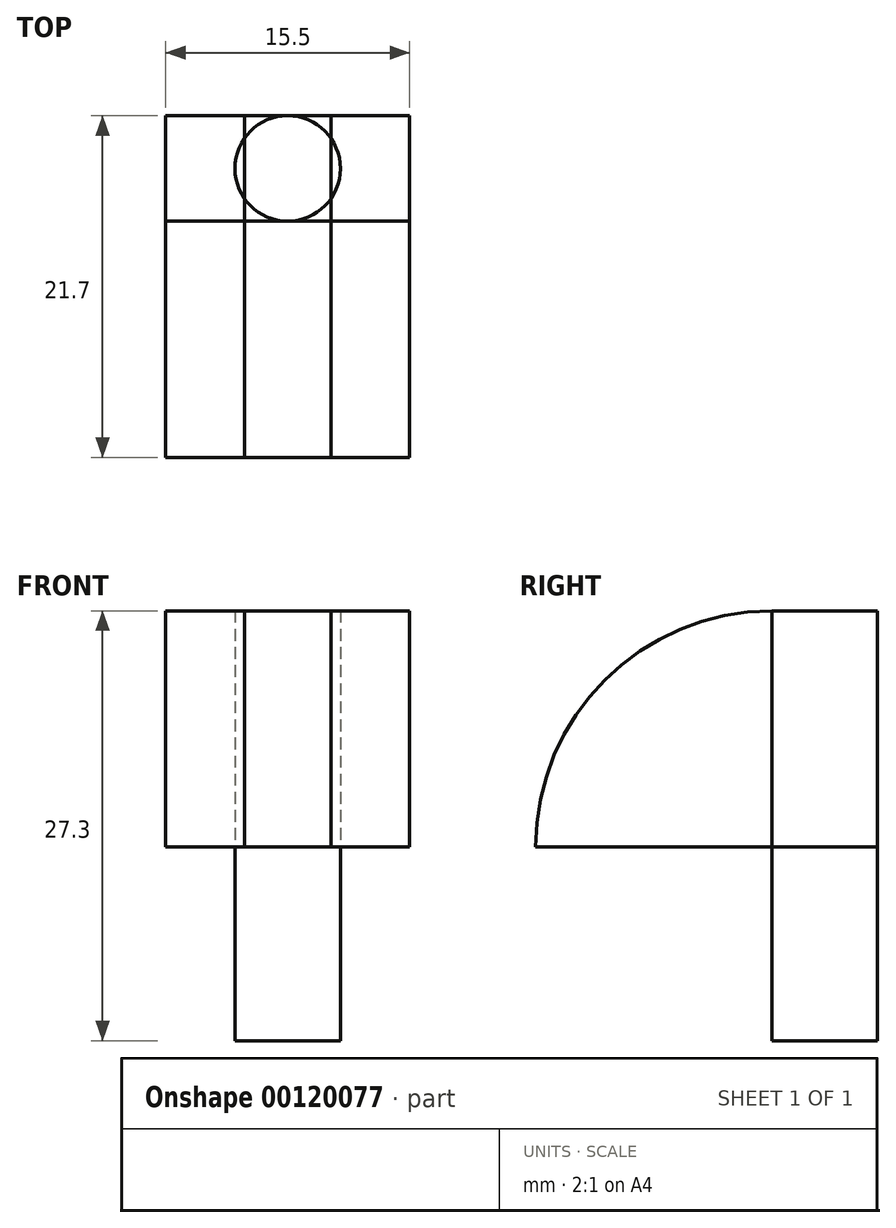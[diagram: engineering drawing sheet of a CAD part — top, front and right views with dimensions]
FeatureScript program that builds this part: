
annotation { "Feature Type Name" : "Feature", "Feature Type Description" : "" }
export const myFeature = defineFeature(function(context is Context, id is Id, definition is map)
    precondition{}
    {
        {
            var Q0;
            Q0=qCreatedBy(makeId("Top.planeOp"),FACE);
            var sketch = newSketch(context, id + "F0", { "sketchPlane" : qUnion([Q0])});
            skCircle(sketch, "E0", {"center": v(0, 0) * mm, "radius": 3.35 * mm});
            skSolve(sketch);
        }
        {
            var Q0;
            Q0 = qSketchRegion(id + "F0", true);
            extrude(context, id + "F1", {"entities" : qUnion([Q0]), "depth" : 15 * mm, "hasSecondDirection" : true, "secondDirectionOppositeDirection" : true, "secondDirectionDepth" : 12.3 * mm});
        }
        {
            var Q0;
            Q0=qCreatedBy(makeId("Front.planeOp"),FACE);
            cPlane(context, id + "F2", {"entities" : qUnion([Q0]), "cplaneType" : CPlaneType.OFFSET, "offset" : 3.35 * mm, "width" : 150 * mm, "height" : 150 * mm});
        }
        {
            var Q0;
            Q0=qCreatedBy(id+"F2.planeOp",FACE);
            var sketch = newSketch(context, id + "F3", { "sketchPlane" : qUnion([Q0])});
            skPoint(sketch, "E1.0", {"position": v(0, 0) * mm});
            skLineSegment(sketch, "E2.bottom", {"start": v(0, 0) * mm, "end": v(2.75, 0) * mm});
            skLineSegment(sketch, "E2.top", {"start": v(0, 15) * mm, "end": v(2.75, 15) * mm});
            skLineSegment(sketch, "E2.left", {"start": v(0, 0) * mm, "end": v(0, 15) * mm});
            skLineSegment(sketch, "E2.right", {"start": v(2.75, 0) * mm, "end": v(2.75, 15) * mm});
            skLineSegment(sketch, "E3.bottom", {"start": v(0, 15) * mm, "end": v(-2.75, 15) * mm});
            skLineSegment(sketch, "E3.top", {"start": v(0, 0) * mm, "end": v(-2.75, 0) * mm});
            skLineSegment(sketch, "E3.left", {"start": v(0, 15) * mm, "end": v(0, 0) * mm});
            skLineSegment(sketch, "E3.right", {"start": v(-2.75, 15) * mm, "end": v(-2.75, 0) * mm});
            skSolve(sketch);
        }
        {
            var Q0;
            Q0=makeQuery(id+"F3.imprint","IMPRINT",FACE,{"disambiguationData":[TD([[makeQuery(id+"F3.imprint","IMPRINT",EDGE,{"derivedFrom":sQuery(id+"F3.wireOp",EDGE,"E2.bottom")}),1.0]])]});
            var Q1;
            Q1=makeQuery(id+"F3.imprint","IMPRINT",FACE,{"disambiguationData":[TD([[makeQuery(id+"F3.imprint","IMPRINT",EDGE,{"derivedFrom":sQuery(id+"F3.wireOp",EDGE,"E3.bottom")}),1.0]])]});
            var Q2;
            Q2=sQuery(id+"F3.wireOp",EDGE,"E2.bottom");
            revolve(context, id + "F4", {"operationType" : NewBodyOperationType.ADD, "entities" : qUnion([Q0, Q1]), "axis" : qUnion([Q2]), "revolveType" : RevolveType.ONE_DIRECTION, "angle" : 90 * degree});
        }
        {
            var Q0;
            Q0=makeQuery(id+"F4.opRevolve","CAP_FACE",FACE,{"disambiguationData":[OSD([sQuery(id+"F3.wireOp",EDGE,"E2.bottom"),sQuery(id+"F3.wireOp",EDGE,"E2.top"),sQuery(id+"F3.wireOp",EDGE,"E2.right"),sQuery(id+"F3.wireOp",EDGE,"E3.bottom"),sQuery(id+"F3.wireOp",EDGE,"E3.top"),sQuery(id+"F3.wireOp",EDGE,"E3.right")])],"isStart":true});
            var Q1;
            Q1=makeQuery(id+"F1.opExtrude","SWEPT_FACE",FACE,{"disambiguationData":[OSD([sQuery(id+"F0.wireOp",EDGE,"E0")])]});
            var Q2;
            Q2=makeQuery(id+"F1.opExtrude","SWEPT_BODY",BODY,{"disambiguationData":[OSD([sQuery(id+"F0.wireOp",EDGE,"E0")])]});
            extrude(context, id + "F5", {"entities" : qUnion([Q0]), "endBoundEntityFace" : qUnion([Q1]), "endBoundEntityBody" : qUnion([Q2]), "depth" : 6.7 * mm});
        }
        {
            var Q0;
            Q0=makeQuery(id+"F5.opExtrude","SWEPT_FACE",FACE,{"disambiguationData":[OSD([sQuery(id+"F3.wireOp",EDGE,"E2.right")])]});
            var Q1;
            Q1=makeQuery(id+"F4.opRevolve","SWEPT_FACE",FACE,{"disambiguationData":[OSD([sQuery(id+"F3.wireOp",EDGE,"E2.right")])]});
            extrude(context, id + "F6", {"entities" : qUnion([Q0, Q1]), "depth" : 5 * mm, "hasSecondDirection" : true, "secondDirectionOppositeDirection" : true, "secondDirectionDepth" : 10.5 * mm});
        }
    });
